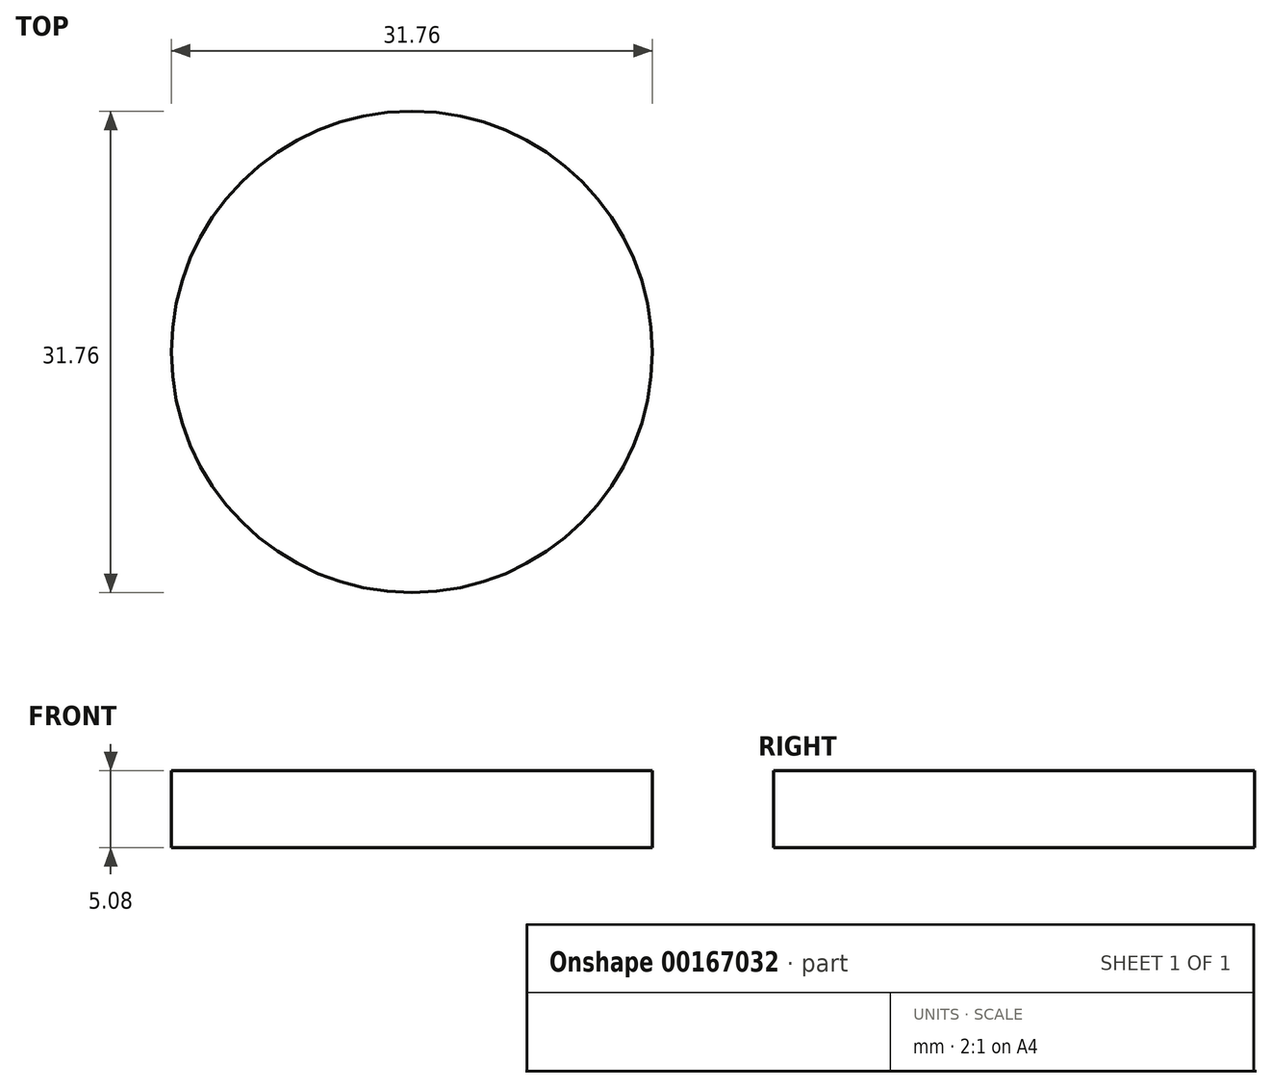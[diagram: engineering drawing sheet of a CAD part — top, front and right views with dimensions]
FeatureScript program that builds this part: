
annotation { "Feature Type Name" : "Feature", "Feature Type Description" : "" }
export const myFeature = defineFeature(function(context is Context, id is Id, definition is map)
    precondition{}
    {
        {
            var Q0;
            Q0=qCreatedBy(makeId("Top.planeOp"),FACE);
            var sketch = newSketch(context, id + "F0", { "sketchPlane" : qUnion([Q0])});
            skCircle(sketch, "E0", {"center": v(0, 0) * mm, "radius": 15.88 * mm});
            skCircle(sketch, "E1", {"center": v(20.21, 2719.23) * mm, "radius": 1086.2 * mm});
            skLineSegment(sketch, "E2", {"start": v(0, -15.88) * mm, "end": v(0, -53.98) * mm});
            skSolve(sketch);
        }
        {
            var Q0;
            Q0=makeQuery(id+"F0.imprint","IMPRINT",FACE,{"disambiguationData":[TD([[makeQuery(id+"F0.imprint","IMPRINT",EDGE,{"derivedFrom":sQuery(id+"F0.wireOp",EDGE,"E0")}),1.0]])]});
            extrude(context, id + "F1", {"entities" : qUnion([Q0]), "depth" : 5.08 * mm});
        }
    });
